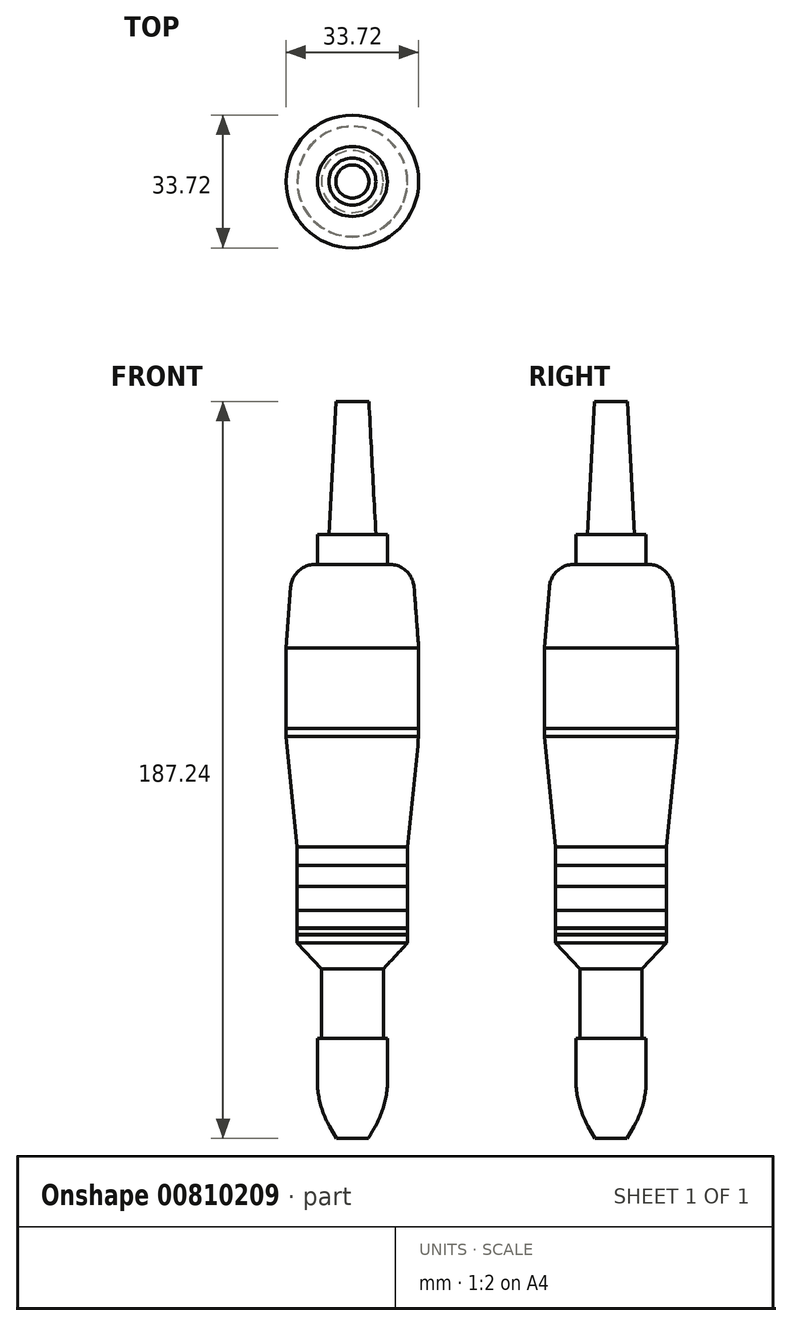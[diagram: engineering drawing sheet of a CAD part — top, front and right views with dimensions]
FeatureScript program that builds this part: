
annotation { "Feature Type Name" : "Feature", "Feature Type Description" : "" }
export const myFeature = defineFeature(function(context is Context, id is Id, definition is map)
    precondition{}
    {
        {
            var Q0;
            Q0=qCreatedBy(makeId("Front.planeOp"),FACE);
            var sketch = newSketch(context, id + "F0", { "sketchPlane" : qUnion([Q0])});
            skLineSegment(sketch, "E0", {"start": v(0, -137.08) * mm, "end": v(0, 175.44) * mm});
            skLineSegment(sketch, "E1", {"start": v(0, -137.08) * mm, "end": v(4.05, -137.08) * mm});
            skLineSegment(sketch, "E2", {"start": v(4.05, -137.08) * mm, "end": v(8.91, -128.58) * mm});
            skLineSegment(sketch, "E3", {"start": v(8.91, -128.58) * mm, "end": v(8.91, -111.65) * mm});
            skLineSegment(sketch, "E4", {"start": v(8.91, -111.65) * mm, "end": v(7.86, -111.65) * mm});
            skLineSegment(sketch, "E5", {"start": v(7.86, -111.65) * mm, "end": v(7.86, -94.03) * mm});
            skLineSegment(sketch, "E6", {"start": v(7.86, -94.03) * mm, "end": v(14.06, -87.4) * mm});
            skLineSegment(sketch, "E7", {"start": v(14.06, -87.4) * mm, "end": v(14.06, -85.37) * mm});
            skLineSegment(sketch, "E8", {"start": v(14.06, -85.37) * mm, "end": v(13.95, -85.37) * mm});
            skLineSegment(sketch, "E9", {"start": v(13.95, -85.37) * mm, "end": v(13.95, -85.3) * mm});
            skLineSegment(sketch, "E10", {"start": v(13.95, -85.3) * mm, "end": v(14.06, -85.3) * mm});
            skLineSegment(sketch, "E11", {"start": v(14.06, -85.3) * mm, "end": v(14.06, -83.72) * mm});
            skLineSegment(sketch, "E12", {"start": v(14.06, -83.72) * mm, "end": v(13.92, -83.72) * mm});
            skLineSegment(sketch, "E13", {"start": v(13.92, -83.72) * mm, "end": v(13.92, -83.64) * mm});
            skLineSegment(sketch, "E14", {"start": v(13.92, -83.64) * mm, "end": v(14.06, -83.64) * mm});
            skLineSegment(sketch, "E15", {"start": v(14.06, -83.64) * mm, "end": v(14.06, -79.17) * mm});
            skLineSegment(sketch, "E16", {"start": v(14.06, -79.17) * mm, "end": v(14.03, -79.17) * mm});
            skLineSegment(sketch, "E17", {"start": v(14.03, -79.17) * mm, "end": v(14.03, -79.14) * mm});
            skLineSegment(sketch, "E18", {"start": v(14.03, -79.14) * mm, "end": v(14.06, -79.14) * mm});
            skLineSegment(sketch, "E19", {"start": v(14.06, -79.14) * mm, "end": v(14.06, -73.09) * mm});
            skLineSegment(sketch, "E20", {"start": v(14.06, -73.09) * mm, "end": v(14, -73.09) * mm});
            skLineSegment(sketch, "E21", {"start": v(14, -73.09) * mm, "end": v(14, -73.03) * mm});
            skLineSegment(sketch, "E22", {"start": v(14, -73.03) * mm, "end": v(14.06, -73.03) * mm});
            skLineSegment(sketch, "E23", {"start": v(14.06, -73.03) * mm, "end": v(14.06, -67.76) * mm});
            skLineSegment(sketch, "E24", {"start": v(14.06, -67.76) * mm, "end": v(14.04, -67.76) * mm});
            skLineSegment(sketch, "E25", {"start": v(14.04, -67.76) * mm, "end": v(14.04, -67.75) * mm});
            skLineSegment(sketch, "E26", {"start": v(14.04, -67.75) * mm, "end": v(14.06, -67.75) * mm});
            skLineSegment(sketch, "E27", {"start": v(14.06, -67.75) * mm, "end": v(14.06, -63.07) * mm});
            skLineSegment(sketch, "E28", {"start": v(14.06, -63.07) * mm, "end": v(16.86, -34.91) * mm});
            skLineSegment(sketch, "E29", {"start": v(16.86, -34.91) * mm, "end": v(16.86, -32.96) * mm});
            skLineSegment(sketch, "E30", {"start": v(16.86, -32.96) * mm, "end": v(16.79, -32.96) * mm});
            skLineSegment(sketch, "E31", {"start": v(16.79, -32.96) * mm, "end": v(16.79, -32.94) * mm});
            skLineSegment(sketch, "E32", {"start": v(16.79, -32.94) * mm, "end": v(16.86, -32.94) * mm});
            skLineSegment(sketch, "E33", {"start": v(16.86, -32.94) * mm, "end": v(16.86, -12.55) * mm});
            skLineSegment(sketch, "E34", {"start": v(16.86, -12.55) * mm, "end": v(15.23, 8.76) * mm});
            skLineSegment(sketch, "E35", {"start": v(15.23, 8.76) * mm, "end": v(0, 8.76) * mm});
            skLineSegment(sketch, "E36", {"start": v(0, 8.76) * mm, "end": v(0, -137.08) * mm});
            skSolve(sketch);
        }
        {
            var Q0;
            Q0=makeQuery(id+"F0.imprint","IMPRINT",FACE,{"disambiguationData":[TD([[makeQuery(id+"F0.imprint","IMPRINT",EDGE,{"derivedFrom":sQuery(id+"F0.wireOp",EDGE,"E1")}),1.0]])]});
            var Q1;
            Q1=sQuery(id+"F0.wireOp",EDGE,"E36");
            revolve(context, id + "F1", {"surfaceOperationType" : NewSurfaceOperationType.NEW, "entities" : qUnion([Q0]), "axis" : qUnion([Q1]), "revolveType" : RevolveType.FULL});
        }
        {
            var Q0;
            Q0=makeQuery(id+"F1.opRevolve","SWEPT_FACE",FACE,{"disambiguationData":[OSD([sQuery(id+"F0.wireOp",EDGE,"E35")])]});
            var sketch = newSketch(context, id + "F2", { "sketchPlane" : qUnion([Q0])});
            skCircle(sketch, "E37", {"center": v(0, 0) * mm, "radius": 8.9 * mm});
            skSolve(sketch);
        }
        {
            var Q0;
            Q0=makeQuery(id+"F2.imprint","IMPRINT",FACE,{"disambiguationData":[TD([[makeQuery(id+"F2.imprint","IMPRINT",EDGE,{"derivedFrom":sQuery(id+"F2.wireOp",EDGE,"E37")}),1.0]])]});
            extrude(context, id + "F3", {"entities" : qUnion([Q0]), "operationType" : NewBodyOperationType.ADD, "depth" : 7.62 * mm, "offsetDistance" : 25.4 * mm});
        }
        {
            var Q0;
            Q0=makeQuery(id+"F3.opExtrude","CAP_FACE",FACE,{"disambiguationData":[OSD([sQuery(id+"F2.wireOp",EDGE,"E37")])],"isStart":false});
            var sketch = newSketch(context, id + "F4", { "sketchPlane" : qUnion([Q0])});
            skCircle(sketch, "E38", {"center": v(0, 0) * mm, "radius": 5.97 * mm});
            skSolve(sketch);
        }
        {
            var Q0;
            Q0 = qSketchRegion(id + "F4", true);
            extrude(context, id + "F5", {"entities" : qUnion([Q0]), "operationType" : NewBodyOperationType.ADD, "depth" : 33.78 * mm, "offsetDistance" : 25.4 * mm, "hasDraft" : true, "draftAngle" : 3 * degree, "draftPullDirection" : true});
        }
        {
            var Q0;
            Q0=makeQuery(id+"F1.opRevolve","SWEPT_EDGE",EDGE,{"disambiguationData":[OSD([sQuery(id+"F0.wireOp",EDGE,"E2"),sQuery(id+"F0.wireOp",EDGE,"E3")])]});
            fillet(context, id + "F6", {"entities" : qUnion([Q0]), "radius" : 23.45 * mm, "tangentPropagation" : true, "allowEdgeOverflow" : false});
        }
        {
            var Q0;
            Q0=makeQuery(id+"F1.opRevolve","SWEPT_FACE",FACE,{"disambiguationData":[OSD([sQuery(id+"F0.wireOp",EDGE,"E1")])]});
            var sketch = newSketch(context, id + "F7", { "sketchPlane" : qUnion([Q0])});
            skCircle(sketch, "E39", {"center": v(0, 0) * mm, "radius": 2.7 * mm});
            skSolve(sketch);
        }
        {
            var Q0;
            Q0 = qSketchRegion(id + "F7", true);
            extrude(context, id + "F8", {"entities" : qUnion([Q0]), "operationType" : NewBodyOperationType.ADD, "oppositeDirection" : true, "depth" : 6.2 * mm, "offsetDistance" : 25.4 * mm});
        }
        {
            var Q0;
            Q0=makeQuery(id+"F1.opRevolve","SWEPT_EDGE",EDGE,{"disambiguationData":[OSD([sQuery(id+"F0.wireOp",EDGE,"E34"),sQuery(id+"F0.wireOp",EDGE,"E35")])]});
            fillet(context, id + "F9", {"entities" : qUnion([Q0]), "radius" : 6.3 * mm, "tangentPropagation" : true, "allowEdgeOverflow" : false});
        }
    });
